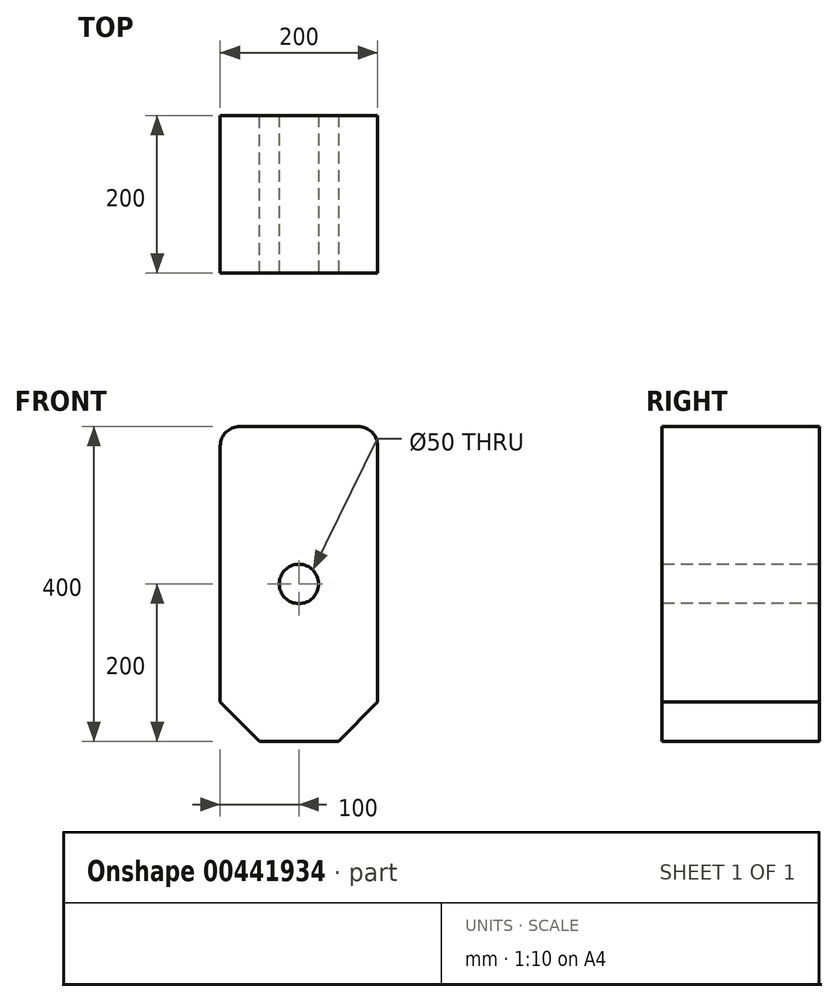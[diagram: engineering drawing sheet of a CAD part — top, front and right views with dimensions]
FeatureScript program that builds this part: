
annotation { "Feature Type Name" : "Feature", "Feature Type Description" : "" }
export const myFeature = defineFeature(function(context is Context, id is Id, definition is map)
    precondition{}
    {
        {
            var Q0;
            Q0=qCreatedBy(makeId("Front.planeOp"),FACE);
            var sketch = newSketch(context, id + "F0", { "sketchPlane" : qUnion([Q0])});
            skLineSegment(sketch, "E0.bottom", {"start": v(100, 200) * mm, "end": v(-100, 200) * mm});
            skLineSegment(sketch, "E0.top", {"start": v(100, -200) * mm, "end": v(-100, -200) * mm});
            skLineSegment(sketch, "E0.left", {"start": v(100, 200) * mm, "end": v(100, -200) * mm});
            skLineSegment(sketch, "E0.right", {"start": v(-100, 200) * mm, "end": v(-100, -200) * mm});
            skPoint(sketch, "E0.middle", {"position": v(0, 0) * mm});
            skSolve(sketch);
        }
        {
            var Q0;
            Q0=makeQuery(id+"F0.imprint","IMPRINT",FACE,{"disambiguationData":[TD([[makeQuery(id+"F0.imprint","IMPRINT",EDGE,{"derivedFrom":sQuery(id+"F0.wireOp",EDGE,"E0.bottom")}),1.0]])]});
            extrude(context, id + "F1", {"entities" : qUnion([Q0]), "depth" : 200 * mm});
        }
        {
            var Q0;
            Q0=makeQuery(id+"F1.opExtrude","CAP_FACE",FACE,{"disambiguationData":[OSD([sQuery(id+"F0.wireOp",EDGE,"E0.bottom"),sQuery(id+"F0.wireOp",EDGE,"E0.top"),sQuery(id+"F0.wireOp",EDGE,"E0.left"),sQuery(id+"F0.wireOp",EDGE,"E0.right")])],"isStart":false});
            var sketch = newSketch(context, id + "F2", { "sketchPlane" : qUnion([Q0])});
            skCircle(sketch, "E1", {"center": v(0, 0) * mm, "radius": 25 * mm});
            skSolve(sketch);
        }
        {
            var Q0;
            Q0=makeQuery(id+"F2.imprint","IMPRINT",FACE,{"disambiguationData":[TD([[makeQuery(id+"F2.imprint","IMPRINT",EDGE,{"derivedFrom":sQuery(id+"F2.wireOp",EDGE,"E1")}),1.0]])]});
            extrude(context, id + "F3", {"entities" : qUnion([Q0]), "operationType" : NewBodyOperationType.REMOVE, "endBound" : BoundingType.THROUGH_ALL, "oppositeDirection" : true, "depth" : 25 * mm});
        }
        {
            var Q0;
            Q0=makeQuery(id+"F1.opExtrude","SWEPT_EDGE",EDGE,{"disambiguationData":[OSD([sQuery(id+"F0.wireOp",EDGE,"E0.top"),sQuery(id+"F0.wireOp",EDGE,"E0.left")])]});
            chamfer(context, id + "F4", {"entities" : qUnion([Q0]), "width" : 50 * mm, "tangentPropagation" : true});
        }
        {
            var Q0;
            Q0=makeQuery(id+"F1.opExtrude","SWEPT_EDGE",EDGE,{"disambiguationData":[OSD([sQuery(id+"F0.wireOp",EDGE,"E0.top"),sQuery(id+"F0.wireOp",EDGE,"E0.right")])]});
            chamfer(context, id + "F5", {"entities" : qUnion([Q0]), "width" : 50 * mm, "tangentPropagation" : true});
        }
        {
            var Q0;
            Q0=makeQuery(id+"F1.opExtrude","SWEPT_EDGE",EDGE,{"disambiguationData":[OSD([sQuery(id+"F0.wireOp",EDGE,"E0.bottom"),sQuery(id+"F0.wireOp",EDGE,"E0.left")])]});
            fillet(context, id + "F6", {"entities" : qUnion([Q0]), "radius" : 25 * mm, "tangentPropagation" : true, "allowEdgeOverflow" : false});
        }
        {
            var Q0;
            Q0=makeQuery(id+"F1.opExtrude","SWEPT_EDGE",EDGE,{"disambiguationData":[OSD([sQuery(id+"F0.wireOp",EDGE,"E0.bottom"),sQuery(id+"F0.wireOp",EDGE,"E0.right")])]});
            fillet(context, id + "F7", {"entities" : qUnion([Q0]), "radius" : 25 * mm, "tangentPropagation" : true, "allowEdgeOverflow" : false});
        }
    });
